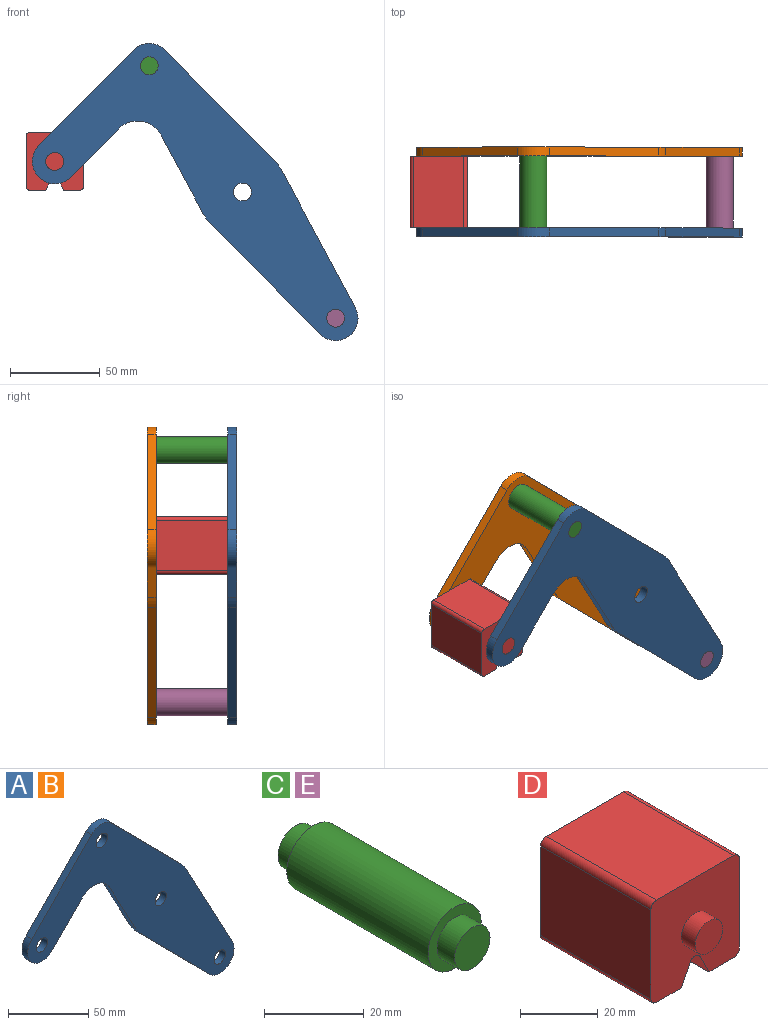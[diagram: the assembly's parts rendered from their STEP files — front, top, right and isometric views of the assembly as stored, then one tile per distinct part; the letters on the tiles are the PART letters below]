
ASSEMBLY  parts=5 mates=3
PART A: 18 faces, bbox 181.7x5x165.8 mm
  f0: plane 43.49x23.35mm, normal (-0.88,0,-0.47), area 246.8mm2, adj f1,f14,f16,f17
  f1: cylinder r=25mm len=5.75mm, axis (0,1,0), area 35.8mm2, adj f0,f2,f16,f17
  f2: plane 61.6x60.87mm, normal (-0.71,0,-0.7), area 433mm2, adj f1,f3,f16,f17
  f3: cylinder r=12.5mm len=21.39mm, axis (0,1,0), area 178.4mm2, adj f2,f4,f16,f17
  f4: plane 76.3x40.96mm, normal (0.88,0,0.47), area 433mm2, adj f3,f5,f16,f17
  f5: cylinder r=25mm len=5.75mm, axis (0,1,0), area 35.8mm2, adj f4,f6,f16,f17
  f6: plane 61.6x60.87mm, normal (0.71,0,0.7), area 433mm2, adj f5,f7,f16,f17
  f7: cylinder r=12.5mm len=17.78mm, axis (0,1,0), area 98.9mm2, adj f6,f8,f16,f17
  f8: plane 53.35x52.71mm, normal (-0.71,0,0.7), area 375mm2, adj f7,f9,f16,f17
  f9: cylinder r=12.5mm len=21.39mm, axis (0,1,0), area 196.3mm2, adj f8,f10,f16,f17
  f10: plane 26.86x26.54mm, normal (0.71,0,-0.7), area 188.8mm2, adj f9,f14,f16,f17
  f11: cylinder r=5mm len=10mm, axis (0,1,0), area 157.1mm2, adj f16,f17
  f12: cylinder r=5mm len=10mm, axis (0,1,0), area 157.1mm2, adj f16,f17
  f13: cylinder r=5mm len=10mm, axis (0,1,0), area 157.1mm2, adj f16,f17
  f14: cylinder r=15mm len=23.89mm, axis (0,1,0), area 140.2mm2, adj f0,f10,f16,f17
  f15: cylinder r=5mm len=10mm, axis (0,1,0), area 157.1mm2, adj f16,f17
  f16: plane 181.66x165.78mm, normal (0,-1,0), area 8710.1mm2, adj f0,f1,f2,f3,f4,f5,f6,f7
  f17: plane 181.66x165.78mm, normal (0,1,0), area 8710.1mm2, adj f0,f1,f2,f3,f4,f5,f6,f7
PART B: same geometry as A
PART C: 7 faces, bbox 15x50x15 mm
  f0: cylinder r=7.5mm len=40mm, axis (0,-1,0), area 1885mm2, adj f2,f5
  f1: cylinder r=5mm len=10mm, axis (0,1,0), area 157.1mm2, adj f2,f3
  f2: plane 15x15mm, normal (0,-1,0), area 98.2mm2, adj f0,f1
  f3: plane 10x10mm, normal (0,-1,0), area 78.5mm2, adj f1
  f4: cylinder r=5mm len=10mm, axis (0,-1,0), area 157.1mm2, adj f5,f6
  f5: plane 15x15mm, normal (0,1,0), area 98.2mm2, adj f0,f4
  f6: plane 10x10mm, normal (0,1,0), area 78.5mm2, adj f4
PART D: 18 faces, bbox 32.1x50x32.1 mm
  f0: plane 40x28.08mm, normal (1,0,0), area 1123.1mm2, adj f4,f10,f13,f14
  f1: plane 40x9.04mm, normal (0,0,-1), area 361.6mm2, adj f2,f4,f10,f14
  f2: plane 40x6.42mm, normal (-0.89,0,-0.45), area 287.2mm2, adj f1,f4,f10,f15
  f3: plane 40x6.42mm, normal (0.89,0,-0.45), area 287.2mm2, adj f4,f5,f10,f15
  f4: plane 32.08x32.08mm, normal (0,-1,0), area 900.6mm2, adj f0,f1,f2,f3,f5,f6,f7,f9
  f5: plane 40x9.04mm, normal (0,0,-1), area 361.6mm2, adj f3,f4,f10,f16
  f6: plane 40x28.08mm, normal (0,0,1), area 1123.1mm2, adj f4,f10,f13,f17
  f7: plane 40x28.08mm, normal (-1,0,0), area 1123.1mm2, adj f4,f10,f16,f17
  f8: plane 10x10mm, normal (0,-1,0), area 78.5mm2, adj f9
  f9: cylinder r=5mm len=10mm, axis (0,1,0), area 157.1mm2, adj f4,f8
  f10: plane 32.08x32.08mm, normal (0,1,0), area 900.6mm2, adj f0,f1,f2,f3,f5,f6,f7,f12
  f11: plane 10x10mm, normal (0,1,0), area 78.5mm2, adj f12
  f12: cylinder r=5mm len=10mm, axis (0,-1,0), area 157.1mm2, adj f10,f11
  f13: cylinder r=2mm len=40mm, axis (0,1,0), area 125.7mm2, adj f0,f4,f6,f10
  f14: cylinder r=2mm len=40mm, axis (0,-1,0), area 125.7mm2, adj f0,f1,f4,f10
  f15: cylinder r=2mm len=40mm, axis (0,1,0), area 177.1mm2, adj f2,f3,f4,f10
  f16: cylinder r=2mm len=40mm, axis (0,1,0), area 125.7mm2, adj f4,f5,f7,f10
  f17: cylinder r=2mm len=40mm, axis (0,-1,0), area 125.7mm2, adj f4,f6,f7,f10
PART E: same geometry as C
PLACE A t=(0,-20,0)mm fixed
PLACE B t=(0,25,0)mm
PLACE C t=(0,-20,0)mm
PLACE D t=(0,-20,0)mm
PLACE E t=(103.95,-20,-140.78)mm
MATE fastened E.f0 <-> A.f3  axis (0,-1,0) through (51.98,-20,-70.39)mm
MATE revolute D.f9 <-> A.f9  axis (0,-1,0) through (-104.69,-20,17.04)mm
MATE fastened B.f7 <-> C.f0  axis (0,-1,0) through (-51.98,20,70.39)mm
